# Revit family: IS_Connect_A9161_BIM_DE
name_source: partatom
category: Plumbing Fixtures
revit_build: Autodesk Revit MEP 2016 (Build: 20161004_0715(x64)
units: mm (PartAtom-declared; Revit-internal decimal feet)

## family parameters
Always vertical = No
Cut with Voids When Loaded = No
OmniClass Number = 23.45.05.14.21.11
OmniClass Title = Bath/Shower Units
Part Type = Normal
Room Calculation Point = No
Round Connector Dimension = Use Diameter
Shared = No
Work Plane-Based = No

## types (1)
- A9161AA CONNECT towel rail
    Accessories = www.idealstandard.de\ersatzteile
    AreaUnits = millimeters
    AssetType = Fixed
    BIMObjectName = ISI_IdealStandard_Furniture_Connect_A9161AA
    BIMobject category = Accessories
    BOSUseNativeGeometries = 1
    BarCode = 4015234824137
    Brand = Ideal Standard
    Brand url = http://www.idealstandard.co.uk
    Color = Chrome
    ConnectionType = Mechanical
    CurrencyUnit = €
    Date of publishing = 06/11/2017
    Description = A9161AA CONNECT towel rail
    DurationUnit = year
    EAN code = https://4015234824137
    Edition number = 1
    ExpectedLife = 25
    Features = CONNECT towel rail
    Finish = Chrome
    IFC Classification = Sanitary Terminal
    IfcExportAs = Sanitary Terminal Type
    IfcExportType = SupportRails
    Installation instructions = http://www.idealstandard.de
    InstallationInstructions = www.idealstandard.de\produkte
    LinearUnits = millimeters
    MainColor = Chrome
    MaintenanceInformation = www.idealstandard.de\produkte
    Manufacturer name = Ideal Standard
    ManufacturerURL = www.idealstandard.com
    Model = A9161AA
    ModelNumber = A9161AA
    ModelReference = CONNECT towel rail
    NBS Reference Code = 85-85
    NBS Reference Description = Support Rails
    Name = Furniture_Connect_A9161AA_IdealStandard
    NettWeight = 1,62 kg
    Nominal height = 221
    Nominal width = 518
    NominalDepth = 251 mm  [stored 0.823491 ft]
    NominalHeight = 221 mm  [stored 0.725066 ft]
    NominalLength = 251 mm  [stored 0.823491 ft]
    NominalWidth = 518 mm  [stored 1.69948 ft]
    OmniClass Code = 23-31 25 00
    OmniClass Description = Toilet and Bath Specialties
    Product Guid = 9b86d64f-035f-470a-a8ea-8ed1e385ec2d
    Product SKU = A9161
    Product data url = https://bimobject.com
    Product family = CONNECT
    Product group = Accessories
    Product name = CONNECT towel rail
    Product url = http://www.idealstandard.de
    ProductInformation = www.idealstandard.de/produkte
    QR code = http://bimobject.com
    Shape = Sculptured
    Size = 518x251x221 mm
    Space = Internal
    SpareParts = www.idealstandard.de/ersatzteile
    Technical description = http://www.idealstandard.de
    URL = www.idealstandard.com
    Uniclass 1.4 Code = L2132
    Uniclass 1.4 Description = Rails
    Uniclass 2.0 Code = PR-85-85
    Uniclass 2.0 Description = Support Rails
    Uniclass 2015 Code = Pr_40_20_76_84
    Uniclass 2015 Name = Support rails
    Uniclass2015Code = Pr_40_20_76_84
    Uniclass2015Title = Support rails
    Uniclass2015Version = Products v1.1
    Version = 1
    VolumeUnits = Litres
    Weight Net (Kg) = 1.62

note: [stored X ft] marks values corroborated as IEEE doubles in the binary element streams (Revit-internal decimal feet)

## geometry (parser evidence)
native form markers: Blend x4, Sweep x1
no freeform markers — native parametric forms only
